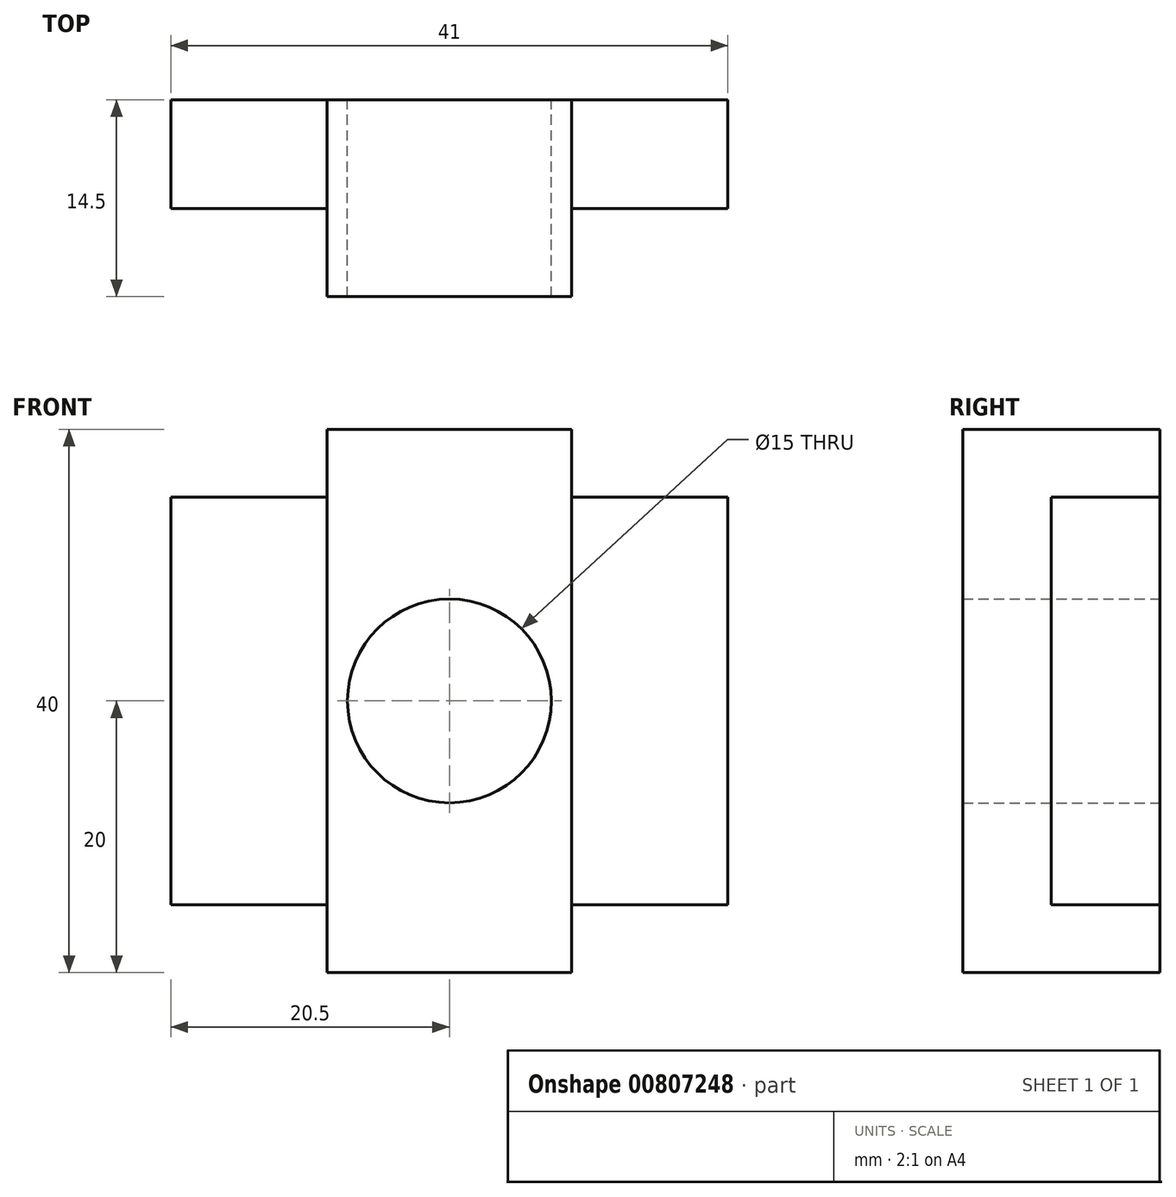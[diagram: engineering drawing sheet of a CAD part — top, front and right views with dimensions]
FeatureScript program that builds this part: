
annotation { "Feature Type Name" : "Feature", "Feature Type Description" : "" }
export const myFeature = defineFeature(function(context is Context, id is Id, definition is map)
    precondition{}
    {
        {
            var Q0;
            Q0=qCreatedBy(makeId("Front.planeOp"),FACE);
            var sketch = newSketch(context, id + "F0", { "sketchPlane" : qUnion([Q0])});
            skCircle(sketch, "E0", {"center": v(0, 0) * mm, "radius": 7.5 * mm});
            skLineSegment(sketch, "E1.bottom", {"start": v(20.5, 15) * mm, "end": v(9, 15) * mm});
            skLineSegment(sketch, "E1.top", {"start": v(20.5, -15) * mm, "end": v(9, -15) * mm});
            skLineSegment(sketch, "E1.left", {"start": v(20.5, 15) * mm, "end": v(20.5, -15) * mm});
            skLineSegment(sketch, "E1.right", {"start": v(-20.5, 15) * mm, "end": v(-20.5, -15) * mm});
            skLineSegment(sketch, "E2.bottom", {"start": v(9, 20) * mm, "end": v(-9, 20) * mm});
            skLineSegment(sketch, "E2.top", {"start": v(9, -20) * mm, "end": v(-9, -20) * mm});
            skLineSegment(sketch, "E2.left", {"start": v(9, 20) * mm, "end": v(9, -20) * mm});
            skLineSegment(sketch, "E2.right", {"start": v(-9, 20) * mm, "end": v(-9, -20) * mm});
            skLineSegment(sketch, "E3.trimOffspring", {"start": v(-9, 15) * mm, "end": v(-20.5, 15) * mm});
            skLineSegment(sketch, "E4.trimOffspring", {"start": v(-9, -15) * mm, "end": v(-20.5, -15) * mm});
            skSolve(sketch);
        }
        {
            var Q0;
            Q0=makeQuery(id+"F0.imprint","IMPRINT",FACE,{"disambiguationData":[TD([[makeQuery(id+"F0.imprint","IMPRINT",EDGE,{"derivedFrom":sQuery(id+"F0.wireOp",EDGE,"E0")}),-1.0]])]});
            extrude(context, id + "F1", {"entities" : qUnion([Q0]), "depth" : 14.5 * mm, "offsetDistance" : 25 * mm});
        }
        {
            var Q0;
            Q0=makeQuery(id+"F0.imprint","IMPRINT",FACE,{"disambiguationData":[TD([[makeQuery(id+"F0.imprint","IMPRINT",EDGE,{"derivedFrom":sQuery(id+"F0.wireOp",EDGE,"E1.right")}),1.0]])]});
            var Q1;
            {var subQ0=sQuery(id+"F0.wireOp",EDGE,"E1.bottom");Q1=makeQuery(id+"F0.imprint","IMPRINT",FACE,{"disambiguationData":[TD([[makeQuery(id+"F0.imprint","IMPRINT",EDGE,{"derivedFrom":subQ0}),1.0]])]});}
            extrude(context, id + "F2", {"entities" : qUnion([Q0, Q1]), "operationType" : NewBodyOperationType.ADD, "depth" : (14.5 - 6.5) * mm, "offsetDistance" : 25 * mm});
        }
    });
